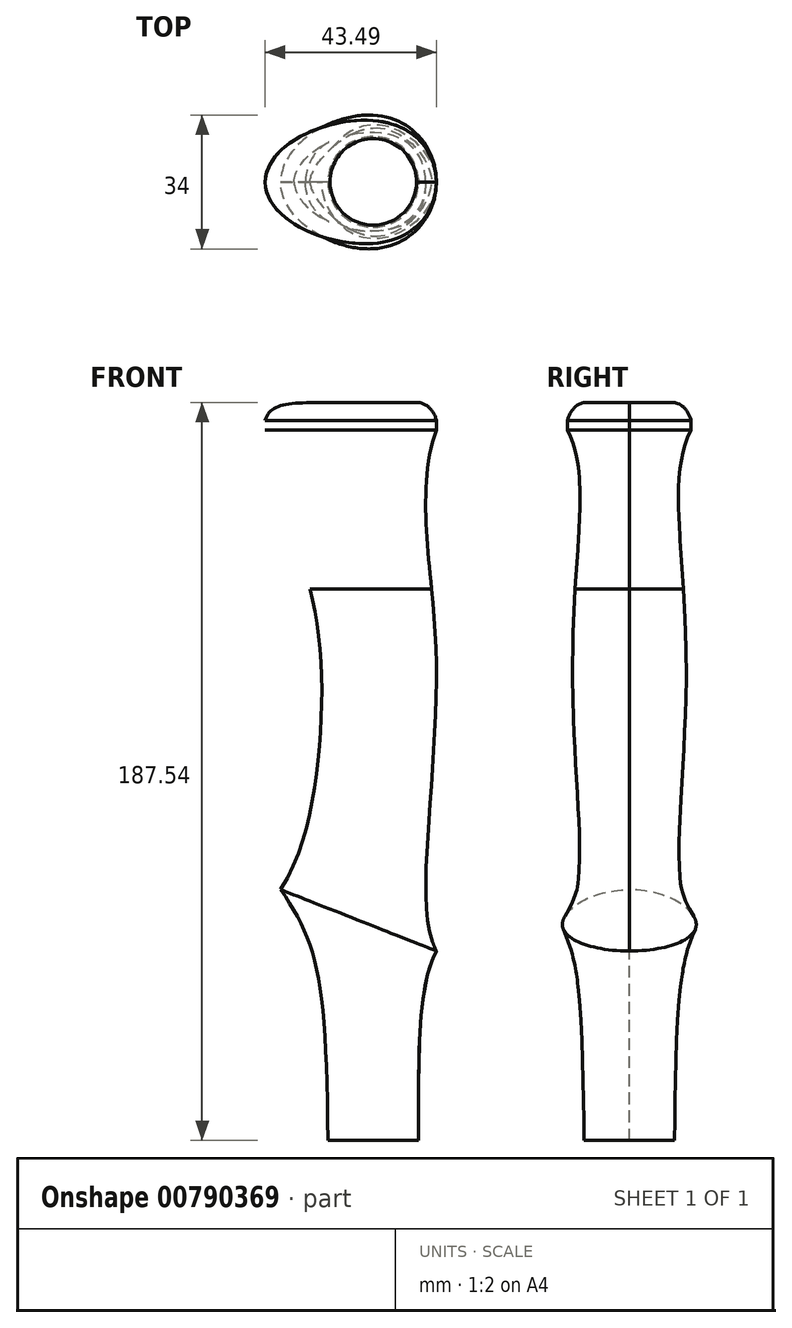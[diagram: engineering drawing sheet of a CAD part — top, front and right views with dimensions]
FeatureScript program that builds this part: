
annotation { "Feature Type Name" : "Feature", "Feature Type Description" : "" }
export const myFeature = defineFeature(function(context is Context, id is Id, definition is map)
    precondition{}
    {
        {
            var Q0;
            Q0=qCreatedBy(makeId("Front.planeOp"),FACE);
            var sketch = newSketch(context, id + "F0", { "sketchPlane" : qUnion([Q0])});
            skLineSegment(sketch, "E0", {"start": v(-17.62, 67.68) * mm, "end": v(-17.62, -122.32) * mm, "construction": true});
            skLineSegment(sketch, "E1", {"start": v(-17.62, -122.32) * mm, "end": v(0.38, -122.32) * mm, "construction": true});
            skLineSegment(sketch, "E2", {"start": v(0.38, -122.32) * mm, "end": v(0.38, 67.68) * mm, "construction": true});
            skLineSegment(sketch, "E3", {"start": v(0.38, 67.68) * mm, "end": v(-17.62, 67.68) * mm, "construction": true});
            skLineSegment(sketch, "E4", {"start": v(0.38, -122.32) * mm, "end": v(2.88, -122.32) * mm, "construction": true});
            skLineSegment(sketch, "E5", {"start": v(-17.62, -122.32) * mm, "end": v(-20.12, -122.32) * mm});
            skFitSpline(sketch, "E6", {"points": [v(2.88, -122.32) * mm, v(7.4, -74.17) * mm], "startDerivative": vector(0.03, 63.14) * mm, "endDerivative": vector(14.5, 27.26) * mm});
            skFitSpline(sketch, "E7", {"points": [v(-20.12, -122.32) * mm, v(-32.13, -58.58) * mm], "startDerivative": vector(-1.09, 124.84) * mm, "endDerivative": vector(-28.22, 40.97) * mm});
            skLineSegment(sketch, "E8", {"start": v(-8.62, 67.68) * mm, "end": v(-8.62, -122.32) * mm, "construction": true});
            skLineSegment(sketch, "E9", {"start": v(-8.62, 65.22) * mm, "end": v(2.38, 65.22) * mm});
            skLineSegment(sketch, "E10", {"start": v(-8.62, 65.22) * mm, "end": v(-19.62, 65.22) * mm});
            skLineSegment(sketch, "E11", {"start": v(-32.13, -58.58) * mm, "end": v(7.4, -74.17) * mm, "construction": true});
            skLineSegment(sketch, "E12", {"start": v(-40.45, 58.12) * mm, "end": v(30.56, 58.12) * mm, "construction": true});
            skFitSpline(sketch, "E13", {"points": [v(7.4, -74.17) * mm, v(5.06, -48.45) * mm, v(7.4, 0) * mm, v(4.88, 33.14) * mm, v(7.4, 58.12) * mm], "startDerivative": vector(-40.78, 85.9) * mm, "endDerivative": vector(35.68, 98.57) * mm});
            skFitSpline(sketch, "E14", {"points": [v(-32.13, -58.58) * mm, v(-23, -28.87) * mm, v(-22.3, 4.14) * mm, v(-26.81, 24.97) * mm, v(-28.67, 31.94) * mm, v(-26.2, 38.16) * mm, v(-36.05, 58.12) * mm], "startDerivative": vector(77.07, 125.37) * mm, "endDerivative": vector(-154.05, 143.53) * mm});
            skLineSegment(sketch, "E15", {"start": v(-38.8, 60.62) * mm, "end": v(16.1, 60.62) * mm, "construction": true});
            skLineSegment(sketch, "E16", {"start": v(-36.05, 58.12) * mm, "end": v(-36.05, 60.62) * mm});
            skLineSegment(sketch, "E17", {"start": v(7.4, 58.12) * mm, "end": v(7.4, 60.62) * mm});
            skFitSpline(sketch, "E18", {"points": [v(-36.05, 60.62) * mm, v(-19.62, 65.22) * mm], "startDerivative": vector(3.87, 13.8) * mm, "endDerivative": vector(30.36, 0.22) * mm});
            skFitSpline(sketch, "E19", {"points": [v(7.4, 60.62) * mm, v(2.38, 65.22) * mm], "startDerivative": vector(-1.37, 7.82) * mm, "endDerivative": vector(-7.08, 0.05) * mm});
            skPoint(sketch, "E20", {"position": v(-8.62, -67.85) * mm});
            skPoint(sketch, "E21", {"position": v(-8.62, 60.62) * mm});
            skPoint(sketch, "E22", {"position": v(-8.62, 58.12) * mm});
            skLineSegment(sketch, "E23", {"start": v(6.21, 17.84) * mm, "end": v(-24.67, 17.84) * mm, "construction": true});
            skPoint(sketch, "E24", {"position": v(-8.62, 17.84) * mm});
            skSolve(sketch);
        }
        {
            var Q0;
            Q0=sQuery(id+"F0.wireOp",EDGE,"E8");
            cPlane(context, id + "F1", {"entities" : qUnion([Q0]), "cplaneType" : CPlaneType.LINE_ANGLE, "offset" : 25 * mm, "angle" : 0 * degree, "width" : 150 * mm, "height" : 150 * mm});
        }
        {
            var Q0;
            Q0=sQuery(id+"F0.wireOp",EDGE,"E11");
            cPlane(context, id + "F2", {"entities" : qUnion([Q0]), "cplaneType" : CPlaneType.LINE_ANGLE, "offset" : 25 * mm, "angle" : 90 * degree, "width" : 150 * mm, "height" : 150 * mm});
        }
        {
            var Q0;
            Q0=qCreatedBy(id+"F2.planeOp",FACE);
            var sketch = newSketch(context, id + "F3", { "sketchPlane" : qUnion([Q0])});
            skPoint(sketch, "E25", {"position": v(16.87, 0) * mm});
            skLineSegment(sketch, "E26", {"start": v(16.87, 0) * mm, "end": v(16.87, -44) * mm, "construction": true});
            skSolve(sketch);
        }
        {
            var Q0;
            Q0=sQuery(id+"F0.wireOp",EDGE,"E1");
            cPlane(context, id + "F4", {"entities" : qUnion([Q0]), "cplaneType" : CPlaneType.LINE_ANGLE, "offset" : 25 * mm, "angle" : 90 * degree, "width" : 150 * mm, "height" : 150 * mm});
        }
        {
            var Q0;
            Q0=qCreatedBy(id+"F1.planeOp",FACE);
            var sketch = newSketch(context, id + "F5", { "sketchPlane" : qUnion([Q0])});
            skPoint(sketch, "E27", {"position": v(0, -122.32) * mm});
            skLineSegment(sketch, "E28", {"start": v(0, -122.32) * mm, "end": v(9, -122.32) * mm, "construction": true});
            skPoint(sketch, "E29", {"position": v(0, 65.22) * mm});
            skLineSegment(sketch, "E30", {"start": v(0, 65.22) * mm, "end": v(11, 65.22) * mm});
            skLineSegment(sketch, "E31", {"start": v(9, 65.22) * mm, "end": v(9, -122.32) * mm, "construction": true});
            skPoint(sketch, "E32", {"position": v(0, 60.62) * mm});
            skPoint(sketch, "E33", {"position": v(0, 58.12) * mm});
            skLineSegment(sketch, "E34", {"start": v(0, 58.12) * mm, "end": v(15.62, 58.12) * mm, "construction": true});
            skLineSegment(sketch, "E35", {"start": v(9, -122.32) * mm, "end": v(11.5, -122.32) * mm});
            skFitSpline(sketch, "E36", {"points": [v(11.5, -122.32) * mm, v(16.97, -67.85) * mm], "startDerivative": vector(1.1, 110.02) * mm, "endDerivative": vector(12.52, 29) * mm});
            skFitSpline(sketch, "E37", {"points": [v(16.97, -67.85) * mm, v(13.14, -58.53) * mm, v(14.48, -6.66) * mm, v(12.57, 37.78) * mm, v(15.62, 58.12) * mm], "startDerivative": vector(-32.24, 48.34) * mm, "endDerivative": vector(40.6, 73.57) * mm});
            skLineSegment(sketch, "E38", {"start": v(15.62, 58.12) * mm, "end": v(15.62, 60.62) * mm});
            skLineSegment(sketch, "E39", {"start": v(15.62, 60.62) * mm, "end": v(0, 60.62) * mm, "construction": true});
            skPoint(sketch, "E40", {"position": v(0, 67.68) * mm});
            skLineSegment(sketch, "E41", {"start": v(9, 65.22) * mm, "end": v(9, 67.68) * mm, "construction": true});
            skLineSegment(sketch, "E42", {"start": v(9, 67.68) * mm, "end": v(0, 67.68) * mm, "construction": true});
            skPoint(sketch, "E43", {"position": v(0, 17.84) * mm});
            skLineSegment(sketch, "E44", {"start": v(0, 17.84) * mm, "end": v(13.73, 17.84) * mm, "construction": true});
            skFitSpline(sketch, "E45", {"points": [v(15.62, 60.62) * mm, v(11, 65.22) * mm], "startDerivative": vector(-1.72, 6.59) * mm, "endDerivative": vector(-7.83, 0.26) * mm});
            skSolve(sketch);
        }
        {
            var Q0;
            Q0=qCreatedBy(id+"F4.planeOp",FACE);
            var sketch = newSketch(context, id + "F6", { "sketchPlane" : qUnion([Q0])});
            skPoint(sketch, "E46", {"position": v(-20.12, 0) * mm});
            skPoint(sketch, "E47", {"position": v(-8.62, -11.5) * mm});
            skPoint(sketch, "E48", {"position": v(2.88, 0) * mm});
            skPoint(sketch, "E49", {"position": v(-8.62, 0) * mm});
            skArc(sketch, "E50", {"start": v(-20.12, 0) * mm, "mid": v(-8.62, -11.5) * mm, "end": v(2.88, 0) * mm});
            skLineSegment(sketch, "E51", {"start": v(2.88, 0) * mm, "end": v(-20.12, 0) * mm});
            skSolve(sketch);
        }
        {
            var Q0;
            Q0=qCreatedBy(id+"F2.planeOp",FACE);
            var sketch = newSketch(context, id + "F7", { "sketchPlane" : qUnion([Q0])});
            skPoint(sketch, "E52", {"position": v(16.87, -16.97) * mm});
            skPoint(sketch, "E53", {"position": v(34.1, 0) * mm});
            skPoint(sketch, "E54", {"position": v(-8.4, 0) * mm});
            skFitSpline(sketch, "E55", {"points": [v(34.1, 0) * mm, v(16.87, -16.97) * mm, v(-8.4, 0) * mm], "startDerivative": vector(0.01, -59.13) * mm, "endDerivative": vector(-0.38, 55.24) * mm});
            skLineSegment(sketch, "E56", {"start": v(34.1, 0) * mm, "end": v(-8.4, 0) * mm});
            skSolve(sketch);
        }
        {
            var Q0;
            Q0=sQuery(id+"F5.wireOp",EDGE,"E34");
            cPlane(context, id + "F8", {"entities" : qUnion([Q0]), "cplaneType" : CPlaneType.LINE_ANGLE, "offset" : 25 * mm, "angle" : 0 * degree, "width" : 150 * mm, "height" : 150 * mm});
        }
        {
            var Q0;
            Q0=makeQuery(id+"F6.imprint","IMPRINT",FACE,{"disambiguationData":[TD([[makeQuery(id+"F6.imprint","IMPRINT",EDGE,{"derivedFrom":sQuery(id+"F6.wireOp",EDGE,"E50")}),1.0]])]});
            var Q1;
            Q1=makeQuery(id+"F7.imprint","IMPRINT",FACE,{"disambiguationData":[TD([[makeQuery(id+"F7.imprint","IMPRINT",EDGE,{"derivedFrom":sQuery(id+"F7.wireOp",EDGE,"E55")}),-1.0]])]});
            var Q2;
            Q2=sQuery(id+"F0.wireOp",EDGE,"E7");
            var Q3;
            Q3=sQuery(id+"F5.wireOp",EDGE,"E36");
            var Q4;
            Q4=sQuery(id+"F0.wireOp",EDGE,"E6");
            loft(context, id + "F9", {"addGuides" : true, "sheetProfilesArray" : [{ "sheetProfileEntities" : qUnion([Q0]) }, { "sheetProfileEntities" : qUnion([Q1]) }], "guidesArray" : [{ "guideEntities" : qUnion([Q2]), "guideDerivativeType" : LoftGuideDerivativeType.DEFAULT, "guideDerivativeMagnitude" : 1 }, { "guideEntities" : qUnion([Q3]), "guideDerivativeType" : LoftGuideDerivativeType.DEFAULT, "guideDerivativeMagnitude" : 1 }, { "guideEntities" : qUnion([Q4]), "guideDerivativeType" : LoftGuideDerivativeType.DEFAULT, "guideDerivativeMagnitude" : 1 }]});
        }
        {
            var Q0;
            Q0=qCreatedBy(id+"F8.planeOp",FACE);
            var sketch = newSketch(context, id + "F10", { "sketchPlane" : qUnion([Q0])});
            skPoint(sketch, "E57", {"position": v(7.4, 0) * mm});
            skPoint(sketch, "E58", {"position": v(-8.62, 15.62) * mm});
            skPoint(sketch, "E59", {"position": v(-36.05, 0) * mm});
            skFitSpline(sketch, "E60", {"points": [v(7.4, 0) * mm, v(-8.62, 15.62) * mm, v(-36.05, 0) * mm], "startDerivative": vector(-0.69, 56.77) * mm, "endDerivative": vector(-0.17, -54.22) * mm});
            skLineSegment(sketch, "E61", {"start": v(7.4, 0) * mm, "end": v(-36.05, 0) * mm});
            skSolve(sketch);
        }
        {
            var Q0;
            Q0=sQuery(id+"F0.wireOp",EDGE,"E23");
            cPlane(context, id + "F11", {"entities" : qUnion([Q0]), "cplaneType" : CPlaneType.LINE_ANGLE, "offset" : 25 * mm, "angle" : 90 * degree, "width" : 150 * mm, "height" : 150 * mm});
        }
        {
            var Q0;
            Q0=qCreatedBy(id+"F11.planeOp",FACE);
            var sketch = newSketch(context, id + "F12", { "sketchPlane" : qUnion([Q0])});
            skPoint(sketch, "E62", {"position": v(-24.67, 0) * mm});
            skPoint(sketch, "E63", {"position": v(-8.62, -13.73) * mm});
            skPoint(sketch, "E64", {"position": v(6.21, 0) * mm});
            skFitSpline(sketch, "E65", {"points": [v(-24.67, 0) * mm, v(-8.62, -13.73) * mm, v(6.21, 0) * mm], "startDerivative": vector(0, -24.2) * mm, "endDerivative": vector(0.28, 36.76) * mm});
            skLineSegment(sketch, "E66", {"start": v(-24.67, 0) * mm, "end": v(6.21, 0) * mm});
            skSolve(sketch);
        }
        {
            var Q1;
            Q1=makeQuery(id+"F7.imprint","IMPRINT",FACE,{"disambiguationData":[TD([[makeQuery(id+"F7.imprint","IMPRINT",EDGE,{"derivedFrom":sQuery(id+"F7.wireOp",EDGE,"E55")}),-1.0]])]});
            var Q2;
            Q2=makeQuery(id+"F12.imprint","IMPRINT",FACE,{"disambiguationData":[TD([[makeQuery(id+"F12.imprint","IMPRINT",EDGE,{"derivedFrom":sQuery(id+"F12.wireOp",EDGE,"E65")}),1.0]])]});
            var Q3;
            Q3=sQuery(id+"F0.wireOp",EDGE,"E14");
            var Q4;
            Q4=sQuery(id+"F5.wireOp",EDGE,"E37");
            var Q5;
            Q5=sQuery(id+"F0.wireOp",EDGE,"E13");
            loft(context, id + "F13", {"operationType" : NewBodyOperationType.ADD, "addGuides" : true, "sheetProfilesArray" : [{ "sheetProfileEntities" : qUnion([Q1]) }, { "sheetProfileEntities" : qUnion([Q2]) }], "guidesArray" : [{ "guideEntities" : qUnion([Q3]), "guideDerivativeType" : LoftGuideDerivativeType.DEFAULT, "guideDerivativeMagnitude" : 1 }, { "guideEntities" : qUnion([Q4]), "guideDerivativeType" : LoftGuideDerivativeType.DEFAULT, "guideDerivativeMagnitude" : 1 }, { "guideEntities" : qUnion([Q5]), "guideDerivativeType" : LoftGuideDerivativeType.DEFAULT, "guideDerivativeMagnitude" : 1 }]});
        }
        {
            var Q1;
            Q1=makeQuery(id+"F13.opLoft","CAP_FACE",FACE,{"disambiguationData":[OSD([makeQuery(id+"F12.imprint","IMPRINT",FACE,{"disambiguationData":[TD([[makeQuery(id+"F12.imprint","IMPRINT",EDGE,{"derivedFrom":sQuery(id+"F12.wireOp",EDGE,"E65")}),1.0]])]})])],"isStart":true});
            var Q2;
            Q2=makeQuery(id+"F10.imprint","IMPRINT",FACE,{"disambiguationData":[TD([[makeQuery(id+"F10.imprint","IMPRINT",EDGE,{"derivedFrom":sQuery(id+"F10.wireOp",EDGE,"E60")}),1.0]])]});
            var Q3;
            Q3=sQuery(id+"F5.wireOp",EDGE,"E37");
            var Q4;
            Q4=sQuery(id+"F0.wireOp",EDGE,"E13");
            var Q5;
            Q5=sQuery(id+"F0.wireOp",EDGE,"E14");
            loft(context, id + "F14", {"operationType" : NewBodyOperationType.ADD, "addGuides" : true, "sheetProfilesArray" : [{ "sheetProfileEntities" : qUnion([Q1]) }, { "sheetProfileEntities" : qUnion([Q2]) }], "guidesArray" : [{ "guideEntities" : qUnion([Q3]), "guideDerivativeType" : LoftGuideDerivativeType.DEFAULT, "guideDerivativeMagnitude" : 1 }, { "guideEntities" : qUnion([Q4]), "guideDerivativeType" : LoftGuideDerivativeType.DEFAULT, "guideDerivativeMagnitude" : 1 }, { "guideEntities" : qUnion([Q5]), "guideDerivativeType" : LoftGuideDerivativeType.DEFAULT, "guideDerivativeMagnitude" : 1 }]});
        }
        {
            var Q0;
            Q0=sQuery(id+"F0.wireOp",EDGE,"E15");
            cPlane(context, id + "F15", {"entities" : qUnion([Q0]), "cplaneType" : CPlaneType.LINE_ANGLE, "offset" : 25 * mm, "angle" : 90 * degree, "width" : 150 * mm, "height" : 150 * mm});
        }
        {
            var Q0;
            Q0=qCreatedBy(id+"F15.planeOp",FACE);
            var sketch = newSketch(context, id + "F16", { "sketchPlane" : qUnion([Q0])});
            skFitSpline(sketch, "E67.MirrorCS", {"points": [v(7.4, 0) * mm, v(-8.62, -15.62) * mm, v(-36.05, 0) * mm], "startDerivative": vector(-0.69, -56.77) * mm, "endDerivative": vector(-0.17, 54.22) * mm});
            skLineSegment(sketch, "E68", {"start": v(-36.05, 0) * mm, "end": v(7.4, 0) * mm});
            skSolve(sketch);
        }
        {
            var Q0;
            Q0=sQuery(id+"F5.wireOp",EDGE,"E30");
            cPlane(context, id + "F17", {"entities" : qUnion([Q0]), "cplaneType" : CPlaneType.LINE_ANGLE, "offset" : 25 * mm, "angle" : 180 * degree, "width" : 150 * mm, "height" : 150 * mm});
        }
        {
            var Q0;
            Q0=qCreatedBy(id+"F17.planeOp",FACE);
            var sketch = newSketch(context, id + "F18", { "sketchPlane" : qUnion([Q0])});
            skPoint(sketch, "E69", {"position": v(-8.62, -11) * mm});
            skPoint(sketch, "E70", {"position": v(2.38, 0) * mm});
            skPoint(sketch, "E71", {"position": v(-19.62, 0) * mm});
            skPoint(sketch, "E72", {"position": v(-8.62, 0) * mm});
            skLineSegment(sketch, "E73", {"start": v(2.38, 0) * mm, "end": v(-19.62, 0) * mm});
            skArc(sketch, "E74", {"start": v(-19.62, 0) * mm, "mid": v(-8.62, -11) * mm, "end": v(2.38, 0) * mm});
            skSolve(sketch);
        }
        {
            var Q1;
            Q1=makeQuery(id+"F10.imprint","IMPRINT",FACE,{"disambiguationData":[TD([[makeQuery(id+"F10.imprint","IMPRINT",EDGE,{"derivedFrom":sQuery(id+"F10.wireOp",EDGE,"E60")}),1.0]])]});
            var Q2;
            Q2=makeQuery(id+"F16.imprint","IMPRINT",FACE,{"disambiguationData":[TD([[makeQuery(id+"F16.imprint","IMPRINT",EDGE,{"derivedFrom":sQuery(id+"F16.wireOp",EDGE,"E67.MirrorCS")}),-1.0]])]});
            loft(context, id + "F19", {"operationType" : NewBodyOperationType.ADD, "sheetProfilesArray" : [{ "sheetProfileEntities" : qUnion([Q1]) }, { "sheetProfileEntities" : qUnion([Q2]) }]});
        }
        {
            var Q1;
            Q1=makeQuery(id+"F16.imprint","IMPRINT",FACE,{"disambiguationData":[TD([[makeQuery(id+"F16.imprint","IMPRINT",EDGE,{"derivedFrom":sQuery(id+"F16.wireOp",EDGE,"E67.MirrorCS")}),-1.0]])]});
            var Q2;
            Q2=makeQuery(id+"F18.imprint","IMPRINT",FACE,{"disambiguationData":[TD([[makeQuery(id+"F18.imprint","IMPRINT",EDGE,{"derivedFrom":sQuery(id+"F18.wireOp",EDGE,"E73")}),1.0]])]});
            var Q3;
            Q3=sQuery(id+"F0.wireOp",EDGE,"E18");
            var Q4;
            Q4=sQuery(id+"F5.wireOp",EDGE,"E45");
            var Q5;
            Q5=sQuery(id+"F0.wireOp",EDGE,"E19");
            loft(context, id + "F20", {"addGuides" : true, "sheetProfilesArray" : [{ "sheetProfileEntities" : qUnion([Q1]) }, { "sheetProfileEntities" : qUnion([Q2]) }], "guidesArray" : [{ "guideEntities" : qUnion([Q3]), "guideDerivativeType" : LoftGuideDerivativeType.DEFAULT, "guideDerivativeMagnitude" : 1 }, { "guideEntities" : qUnion([Q4]), "guideDerivativeType" : LoftGuideDerivativeType.DEFAULT, "guideDerivativeMagnitude" : 1 }, { "guideEntities" : qUnion([Q5]), "guideDerivativeType" : LoftGuideDerivativeType.DEFAULT, "guideDerivativeMagnitude" : 1 }]});
        }
        {
            var Q0;
            Q0=makeQuery(id+"F20.opLoft","SWEPT_BODY",BODY,{"disambiguationData":[OSD([sQuery(id+"F0.wireOp",EDGE,"E18"),sQuery(id+"F0.wireOp",EDGE,"E19"),sQuery(id+"F5.wireOp",EDGE,"E45"),makeQuery(id+"F16.imprint","IMPRINT",FACE,{"disambiguationData":[TD([[makeQuery(id+"F16.imprint","IMPRINT",EDGE,{"derivedFrom":sQuery(id+"F16.wireOp",EDGE,"E67.MirrorCS")}),-1.0]])]}),makeQuery(id+"F18.imprint","IMPRINT",FACE,{"disambiguationData":[TD([[makeQuery(id+"F18.imprint","IMPRINT",EDGE,{"derivedFrom":sQuery(id+"F18.wireOp",EDGE,"E73")}),1.0]])]})])]});
            deleteBodies(context, id + "F21", {"entities" : qUnion([Q0])});
        }
        {
            var Q1;
            Q1=makeQuery(id+"F16.imprint","IMPRINT",FACE,{"disambiguationData":[TD([[makeQuery(id+"F16.imprint","IMPRINT",EDGE,{"derivedFrom":sQuery(id+"F16.wireOp",EDGE,"E67.MirrorCS")}),-1.0]])]});
            var Q2;
            Q2=makeQuery(id+"F18.imprint","IMPRINT",FACE,{"disambiguationData":[TD([[makeQuery(id+"F18.imprint","IMPRINT",EDGE,{"derivedFrom":sQuery(id+"F18.wireOp",EDGE,"E73")}),1.0]])]});
            var Q3;
            Q3=sQuery(id+"F5.wireOp",EDGE,"E45");
            var Q4;
            Q4=sQuery(id+"F0.wireOp",EDGE,"E19");
            var Q5;
            Q5=sQuery(id+"F0.wireOp",EDGE,"E18");
            loft(context, id + "F22", {"operationType" : NewBodyOperationType.ADD, "addGuides" : true, "sheetProfilesArray" : [{ "sheetProfileEntities" : qUnion([Q1]) }, { "sheetProfileEntities" : qUnion([Q2]) }], "guidesArray" : [{ "guideEntities" : qUnion([Q3]), "guideDerivativeType" : LoftGuideDerivativeType.DEFAULT, "guideDerivativeMagnitude" : 1 }, { "guideEntities" : qUnion([Q4]), "guideDerivativeType" : LoftGuideDerivativeType.DEFAULT, "guideDerivativeMagnitude" : 1 }, { "guideEntities" : qUnion([Q5]), "guideDerivativeType" : LoftGuideDerivativeType.DEFAULT, "guideDerivativeMagnitude" : 1 }]});
        }
        {
            var Q0;
            Q0=makeQuery(id+"F9.opLoft","SWEPT_BODY",BODY,{"disambiguationData":[OSD([sQuery(id+"F0.wireOp",EDGE,"E6"),sQuery(id+"F0.wireOp",EDGE,"E7"),sQuery(id+"F5.wireOp",EDGE,"E36"),makeQuery(id+"F6.imprint","IMPRINT",FACE,{"disambiguationData":[TD([[makeQuery(id+"F6.imprint","IMPRINT",EDGE,{"derivedFrom":sQuery(id+"F6.wireOp",EDGE,"E50")}),1.0]])]}),makeQuery(id+"F7.imprint","IMPRINT",FACE,{"disambiguationData":[TD([[makeQuery(id+"F7.imprint","IMPRINT",EDGE,{"derivedFrom":sQuery(id+"F7.wireOp",EDGE,"E55")}),-1.0]])]})])]});
            var Q1;
            Q1=qCreatedBy(makeId("Front.planeOp"),FACE);
            mirror(context, id + "F23", {"operationType" : NewBodyOperationType.ADD, "entities" : qUnion([Q0]), "mirrorPlane" : qUnion([Q1])});
        }
    });
